# Revit family: S36-PDx149-xxFSW8xxLPOxxxx
name_source: partatom
category: Leuchten
revit_build: Autodesk Revit 2017 (Build: 20190508_0315(x64)
units: mm (PartAtom-declared; Revit-internal decimal feet)

## family parameters
Basisbauteil = Fläche
Beim Laden mit Abzugskörper schneiden = Nein
Bemaßung runder Anschluss = Durchmesser verwenden
Gemeinsam genutzt = Nein
Lichtquelle = Ja
OmniClass-Nummer = 23.80.70.11
OmniClass-Titel = Luminaries for Internal Lighting
Raumberechnungspunkt = Nein
Teiletyp = Normal

## types (9) — shared parameters
Baugruppenkennzeichen = D5020200
Emissionsform beim Rendern sichtbar = Nein
Farbfilter = 16777215
Farbtemperaturverschiebung bei Dämpfen der Lampe = <Keine Auswahl>
Hersteller = Spectral
Lampe = LED
Neigungswinkel = 90.00°
URL = https://www.spectral-lighting.com
Von Breite des Rechtecks ausssenden = 1487 mm  [stored 4.87861 ft]
Von Länge des Rechtecks aussenden = 36 mm  [stored 0.11811 ft]
brand = Spectral
conformity mark = CE
electrical safety class = 1
height = 72 mm  [stored 0.23622 ft]
ingress protection (IP) code = IP20
length = 1490 mm  [stored 4.88845 ft]
nominal frequency = 50-60Hz
nominal voltage = 230
voltage type (AC, DC, UC) = AC
weight = 3.7 kg
width = 36 mm  [stored 0.11811 ft]
zero-valued in all types: Vorgabe-Ansicht

## per-type parameters (varying)
| type | Datei für fotometrisches Netz | Modell | Scheinlast | rated input power |
| S36-PD149 NDFSW830LPO0300 | S36-PD149 DAFWS840LPO0300.IES | SPG0620057AQ | 27 VA | 27 |
| S36-PD149 DAFSW830LPO0300 | S36-PD149 DAFWS840LPO0300.IES | SPG0630057AQ | 27 VA | 27 |
| S36-PD149 NDFSW840LPO0300 | S36-PD149 DAFWS840LPO0300.IES | SPG0620039AQ | 27 VA | 27 |
| S36-PD149 DAFSW840LPO0300 | S36-PD149 DAFWS840LPO0300.IES | SPG0630039AQ | 27 VA | 27 |
| S36-PDI149 NDFSW830LPO0700 | S36-PDI149 DAFWS840LPO0700.IES | SPG0620063AQ | 54 VA | 54 |
| S36-PDI149 DAFSW830LPO0700 | S36-PDI149 DAFWS840LPO0700.IES | SPG0630063AQ | 54 VA | 54 |
| S36-PDI149 NDFSW840LPO0700 | S36-PDI149 DAFWS840LPO0700.IES | SPG0620033AQ | 54 VA | 54 |
| S36-PDI149 DAFSW840LPO0700 | S36-PDI149 DAFWS840LPO0700.IES | SPG0630033AQ | 54 VA | 54 |
| S36-PD149 DAFSWTWLPO0300 | S36-PD149 DAFWS840LPO0300.IES | SPG0630087AQ | 27 VA | 27 |

note: column(s) folded — value = type name in every type: product name

note: [stored X ft] marks values corroborated as IEEE doubles in the binary element streams (Revit-internal decimal feet)
